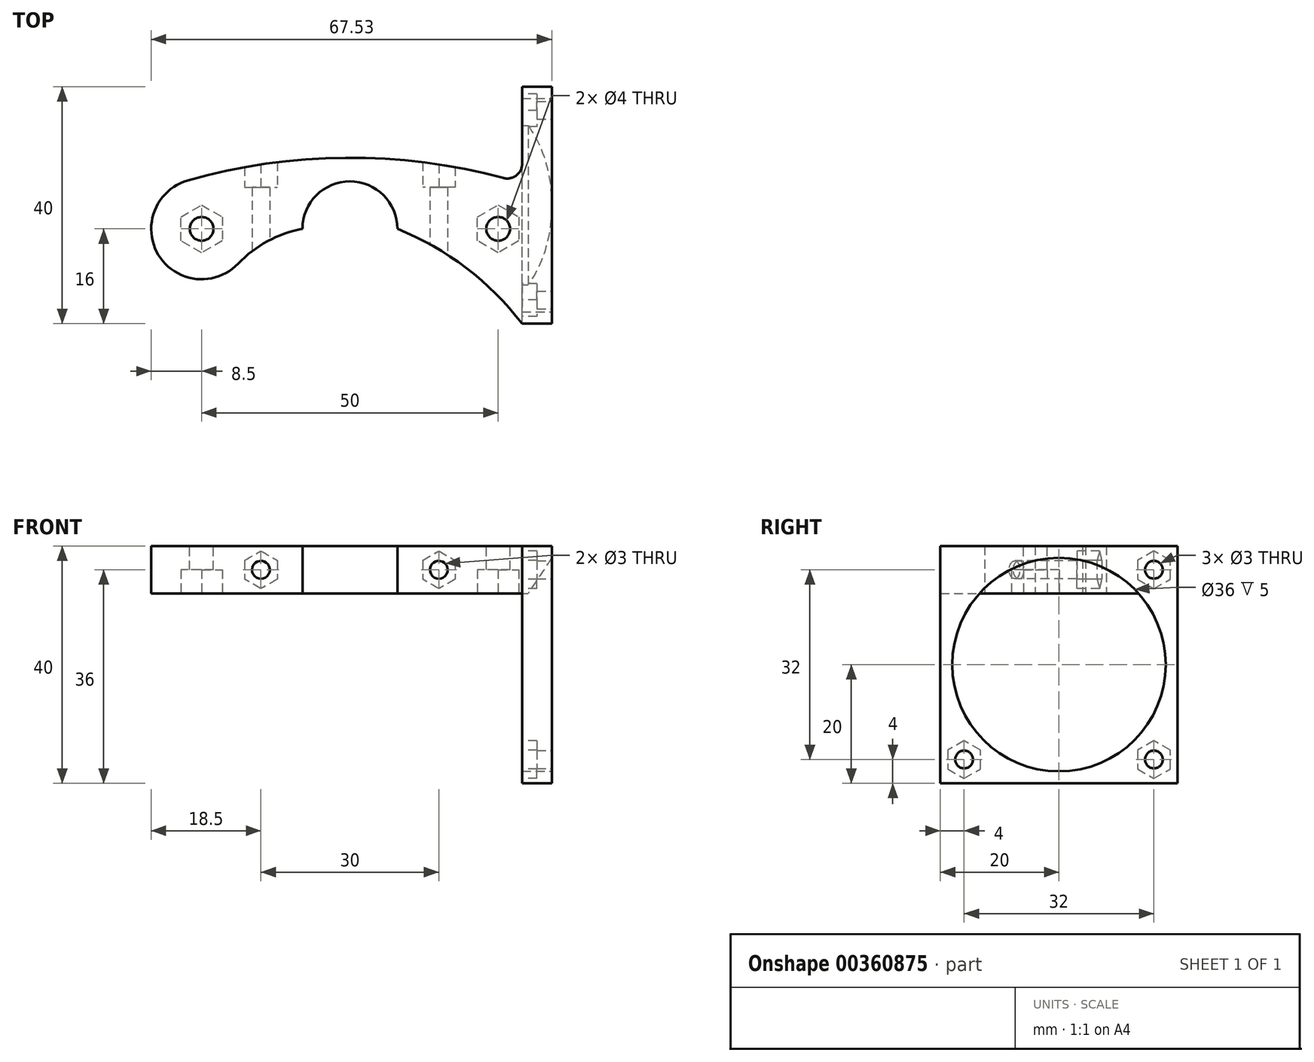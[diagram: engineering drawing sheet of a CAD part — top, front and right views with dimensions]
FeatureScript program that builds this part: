
annotation { "Feature Type Name" : "Feature", "Feature Type Description" : "" }
export const myFeature = defineFeature(function(context is Context, id is Id, definition is map)
    precondition{}
    {
        {
            var Q0;
            Q0=qCreatedBy(makeId("Top.planeOp"),FACE);
            var sketch = newSketch(context, id + "F0", { "sketchPlane" : qUnion([Q0])});
            skArc(sketch, "E0", {"start": v(8, 0) * mm, "mid": v(0, 8) * mm, "end": v(-8, 0) * mm});
            skCircle(sketch, "E1.cCircle", {"center": v(-25, 0) * mm, "radius": 3.5 * mm, "construction": true});
            skLineSegment(sketch, "E1.0", {"start": v(-21.5, 2.02) * mm, "end": v(-21.5, -2.02) * mm});
            skLineSegment(sketch, "E1.1", {"start": v(-21.5, -2.02) * mm, "end": v(-25, -4.04) * mm});
            skLineSegment(sketch, "E1.2", {"start": v(-25, -4.04) * mm, "end": v(-28.5, -2.02) * mm});
            skLineSegment(sketch, "E1.3", {"start": v(-28.5, -2.02) * mm, "end": v(-28.5, 2.02) * mm});
            skLineSegment(sketch, "E1.4", {"start": v(-28.5, 2.02) * mm, "end": v(-25, 4.04) * mm});
            skLineSegment(sketch, "E1.5", {"start": v(-25, 4.04) * mm, "end": v(-21.5, 2.02) * mm});
            skPoint(sketch, "E1.0.midPoint", {"position": v(-21.5, 0) * mm});
            skCircle(sketch, "E2.cCircle", {"center": v(25, 0) * mm, "radius": 3.5 * mm, "construction": true});
            skLineSegment(sketch, "E2.0", {"start": v(28.5, 2.02) * mm, "end": v(28.5, -2.02) * mm});
            skLineSegment(sketch, "E2.1", {"start": v(28.5, -2.02) * mm, "end": v(25, -4.04) * mm});
            skLineSegment(sketch, "E2.2", {"start": v(25, -4.04) * mm, "end": v(21.5, -2.02) * mm});
            skLineSegment(sketch, "E2.3", {"start": v(21.5, -2.02) * mm, "end": v(21.5, 2.02) * mm});
            skLineSegment(sketch, "E2.4", {"start": v(21.5, 2.02) * mm, "end": v(25, 4.04) * mm});
            skLineSegment(sketch, "E2.5", {"start": v(25, 4.04) * mm, "end": v(28.5, 2.02) * mm});
            skPoint(sketch, "E2.0.midPoint", {"position": v(28.5, 0) * mm});
            skCircle(sketch, "E3", {"center": v(-25, 0) * mm, "radius": 8.5 * mm});
            skCircle(sketch, "E4", {"center": v(25, 0) * mm, "radius": 8.5 * mm});
            skLineSegment(sketch, "E5", {"start": v(0, 0) * mm, "end": v(0, 12) * mm});
            skArc(sketch, "E6", {"start": v(27.33, 8.17) * mm, "mid": v(0, 12) * mm, "end": v(-27.33, 8.17) * mm});
            skPoint(sketch, "E6.first.point", {"position": v(-27.33, 8.17) * mm});
            skPoint(sketch, "E6.second.point", {"position": v(27.33, 8.17) * mm});
            skLineSegment(sketch, "E7.bottom", {"start": v(29.03, 24) * mm, "end": v(34.03, 24) * mm});
            skLineSegment(sketch, "E7.top", {"start": v(29.03, -16) * mm, "end": v(34.03, -16) * mm});
            skLineSegment(sketch, "E7.left", {"start": v(29.03, 24) * mm, "end": v(29.03, -16) * mm});
            skLineSegment(sketch, "E7.right", {"start": v(34.03, 24) * mm, "end": v(34.03, -16) * mm});
            skArc(sketch, "E8", {"start": v(29.03, -16) * mm, "mid": v(19.6, -6.57) * mm, "end": v(8, 0) * mm});
            skPoint(sketch, "E8.third.point", {"position": v(19.9, -6.8) * mm});
            skArc(sketch, "E9", {"start": v(25.88, 8.58) * mm, "mid": v(28.05, 9) * mm, "end": v(29.03, 11) * mm});
            skArc(sketch, "E10", {"start": v(-8, 0) * mm, "mid": v(-13.89, -2.08) * mm, "end": v(-18.85, -5.87) * mm});
            skSolve(sketch);
        }
        {
            var Q0;
            Q0 = qSketchRegion(id + "F0", true);
            var Q1;
            {var subQ0=sQuery(id+"F0.wireOp",EDGE,"E7.left");var subQ1=sQuery(id+"F0.wireOp",EDGE,"E4");var subQ2=makeQuery(id+"F0.imprint","INTERSECT",VERTEX,{"disambiguationData":[OD(0.0)],"derivedFrom":[subQ1,subQ0]});Q1=makeQuery(id+"F0.imprint","IMPRINT",FACE,{"disambiguationData":[TD([[makeQuery(id+"F0.imprint","IMPRINT",EDGE,{"disambiguationData":[TD([[subQ2,1.0]])],"derivedFrom":subQ1}),1.0]])]});}
            extrude(context, id + "F1", {"entities" : qUnion([Q0, Q1]), "depth" : 8 * mm});
        }
        {
            var Q0;
            Q0=makeQuery(id+"F1.opExtrude","CAP_FACE",FACE,{"disambiguationData":[OSD([sQuery(id+"F0.wireOp",EDGE,"E0"),sQuery(id+"F0.wireOp",EDGE,"E1.0"),sQuery(id+"F0.wireOp",EDGE,"E1.1"),sQuery(id+"F0.wireOp",EDGE,"E1.2"),sQuery(id+"F0.wireOp",EDGE,"E1.3"),sQuery(id+"F0.wireOp",EDGE,"E1.4"),sQuery(id+"F0.wireOp",EDGE,"E1.5"),sQuery(id+"F0.wireOp",EDGE,"E2.0"),sQuery(id+"F0.wireOp",EDGE,"E2.1"),sQuery(id+"F0.wireOp",EDGE,"E2.2"),sQuery(id+"F0.wireOp",EDGE,"E2.3"),sQuery(id+"F0.wireOp",EDGE,"E2.4"),sQuery(id+"F0.wireOp",EDGE,"E2.5"),sQuery(id+"F0.wireOp",EDGE,"E3"),sQuery(id+"F0.wireOp",EDGE,"E6"),sQuery(id+"F0.wireOp",EDGE,"E7.bottom"),sQuery(id+"F0.wireOp",EDGE,"E7.top"),sQuery(id+"F0.wireOp",EDGE,"E7.left"),sQuery(id+"F0.wireOp",EDGE,"E7.right"),sQuery(id+"F0.wireOp",EDGE,"E8"),sQuery(id+"F0.wireOp",EDGE,"E9"),sQuery(id+"F0.wireOp",EDGE,"E10")])],"isStart":false});
            var sketch = newSketch(context, id + "F2", { "sketchPlane" : qUnion([Q0])});
            skCircle(sketch, "E11.cCircle", {"center": v(25, 0) * mm, "radius": 3.5 * mm, "construction": true});
            skPoint(sketch, "E11.cCircle.centerSnap0", {"position": v(21.5, 0) * mm});
            skLineSegment(sketch, "E11.0", {"start": v(28.5, 2.02) * mm, "end": v(28.5, -2.02) * mm});
            skLineSegment(sketch, "E11.1", {"start": v(28.5, -2.02) * mm, "end": v(25, -4.04) * mm});
            skLineSegment(sketch, "E11.2", {"start": v(25, -4.04) * mm, "end": v(21.5, -2.02) * mm});
            skLineSegment(sketch, "E11.3", {"start": v(21.5, -2.02) * mm, "end": v(21.5, 2.02) * mm});
            skLineSegment(sketch, "E11.4", {"start": v(21.5, 2.02) * mm, "end": v(25, 4.04) * mm});
            skLineSegment(sketch, "E11.5", {"start": v(25, 4.04) * mm, "end": v(28.5, 2.02) * mm});
            skPoint(sketch, "E11.0.midPoint", {"position": v(28.5, 0) * mm});
            skCircle(sketch, "E12.cCircle", {"center": v(-25, 0) * mm, "radius": 3.5 * mm, "construction": true});
            skLineSegment(sketch, "E12.0", {"start": v(-21.5, 2.02) * mm, "end": v(-21.5, -2.02) * mm});
            skLineSegment(sketch, "E12.1", {"start": v(-21.5, -2.02) * mm, "end": v(-25, -4.04) * mm});
            skLineSegment(sketch, "E12.2", {"start": v(-25, -4.04) * mm, "end": v(-28.5, -2.02) * mm});
            skLineSegment(sketch, "E12.3", {"start": v(-28.5, -2.02) * mm, "end": v(-28.5, 2.02) * mm});
            skLineSegment(sketch, "E12.4", {"start": v(-28.5, 2.02) * mm, "end": v(-25, 4.04) * mm});
            skLineSegment(sketch, "E12.5", {"start": v(-25, 4.04) * mm, "end": v(-21.5, 2.02) * mm});
            skPoint(sketch, "E12.0.midPoint", {"position": v(-21.5, 0) * mm});
            skCircle(sketch, "E13", {"center": v(-25, 0) * mm, "radius": 2 * mm});
            skCircle(sketch, "E14", {"center": v(25, 0) * mm, "radius": 2 * mm});
            skSolve(sketch);
        }
        {
            var Q0;
            Q0 = qSketchRegion(id + "F2", true);
            extrude(context, id + "F3", {"entities" : qUnion([Q0]), "operationType" : NewBodyOperationType.ADD, "oppositeDirection" : true, "depth" : 4 * mm});
        }
        {
            var Q0;
            Q0=makeQuery(id+"F1.opExtrude","CAP_FACE",FACE,{"disambiguationData":[OSD([sQuery(id+"F0.wireOp",EDGE,"E0"),sQuery(id+"F0.wireOp",EDGE,"E1.0"),sQuery(id+"F0.wireOp",EDGE,"E1.1"),sQuery(id+"F0.wireOp",EDGE,"E1.2"),sQuery(id+"F0.wireOp",EDGE,"E1.3"),sQuery(id+"F0.wireOp",EDGE,"E1.4"),sQuery(id+"F0.wireOp",EDGE,"E1.5"),sQuery(id+"F0.wireOp",EDGE,"E2.0"),sQuery(id+"F0.wireOp",EDGE,"E2.1"),sQuery(id+"F0.wireOp",EDGE,"E2.2"),sQuery(id+"F0.wireOp",EDGE,"E2.3"),sQuery(id+"F0.wireOp",EDGE,"E2.4"),sQuery(id+"F0.wireOp",EDGE,"E2.5"),sQuery(id+"F0.wireOp",EDGE,"E3"),sQuery(id+"F0.wireOp",EDGE,"E6"),sQuery(id+"F0.wireOp",EDGE,"E7.bottom"),sQuery(id+"F0.wireOp",EDGE,"E7.top"),sQuery(id+"F0.wireOp",EDGE,"E7.left"),sQuery(id+"F0.wireOp",EDGE,"E7.right"),sQuery(id+"F0.wireOp",EDGE,"E8"),sQuery(id+"F0.wireOp",EDGE,"E9"),sQuery(id+"F0.wireOp",EDGE,"E10")])],"isStart":true});
            var sketch = newSketch(context, id + "F4", { "sketchPlane" : qUnion([Q0])});
            skLineSegment(sketch, "E15.bottom", {"start": v(29.03, 16) * mm, "end": v(34.03, 16) * mm});
            skLineSegment(sketch, "E15.top", {"start": v(29.03, -24) * mm, "end": v(34.03, -24) * mm});
            skLineSegment(sketch, "E15.left", {"start": v(29.03, 16) * mm, "end": v(29.03, -24) * mm});
            skLineSegment(sketch, "E15.right", {"start": v(34.03, 16) * mm, "end": v(34.03, -24) * mm});
            skSolve(sketch);
        }
        {
            var Q0;
            Q0 = qSketchRegion(id + "F4", true);
            extrude(context, id + "F5", {"entities" : qUnion([Q0]), "operationType" : NewBodyOperationType.ADD, "depth" : 32 * mm});
        }
        {
            var Q0;
            Q0=makeQuery(id+"F5.boolean.opBoolean","MERGE",FACE,{"derivedFrom":[makeQuery(id+"F1.opExtrude","SWEPT_FACE",FACE,{"disambiguationData":[OSD([sQuery(id+"F0.wireOp",EDGE,"E7.right")])]}),makeQuery(id+"F5.opExtrude","SWEPT_FACE",FACE,{"disambiguationData":[OSD([sQuery(id+"F4.wireOp",EDGE,"E15.right")])]})]});
            var sketch = newSketch(context, id + "F6", { "sketchPlane" : qUnion([Q0])});
            skLineSegment(sketch, "E16", {"start": v(-16, 8) * mm, "end": v(24, -32) * mm});
            skLineSegment(sketch, "E17", {"start": v(24, 8) * mm, "end": v(-16, -32) * mm});
            skCircle(sketch, "E18", {"center": v(4, -12) * mm, "radius": 18 * mm});
            skSolve(sketch);
        }
        {
            var Q0;
            Q0=qCreatedBy(makeId("Front.planeOp"),FACE);
            var sketch = newSketch(context, id + "F7", { "sketchPlane" : qUnion([Q0])});
            skLineSegment(sketch, "E19", {"start": v(-15, 0) * mm, "end": v(-15, 8) * mm});
            skCircle(sketch, "E20", {"center": v(-15, 4) * mm, "radius": 1.5 * mm});
            skPoint(sketch, "E20.perimeterSnap0", {"position": v(-15, 4) * mm});
            skLineSegment(sketch, "E21", {"start": v(15, 0) * mm, "end": v(15, 8) * mm});
            skCircle(sketch, "E22", {"center": v(15, 4) * mm, "radius": 1.5 * mm});
            skPoint(sketch, "E22.perimeterSnap0", {"position": v(15, 4) * mm});
            skSolve(sketch);
        }
        {
            var Q0;
            Q0 = qSketchRegion(id + "F7", true);
            extrude(context, id + "F8", {"entities" : qUnion([Q0]), "operationType" : NewBodyOperationType.REMOVE, "endBound" : BoundingType.SYMMETRIC, "oppositeDirection" : true, "depth" : 25 * mm});
        }
        {
            var Q0;
            Q0=qCreatedBy(makeId("Front.planeOp"),FACE);
            cPlane(context, id + "F9", {"entities" : qUnion([Q0]), "cplaneType" : CPlaneType.OFFSET, "offset" : 7 * mm, "oppositeDirection" : true, "width" : 150 * mm, "height" : 150 * mm});
        }
        {
            var Q0;
            Q0=qCreatedBy(id+"F9.planeOp",FACE);
            var sketch = newSketch(context, id + "F10", { "sketchPlane" : qUnion([Q0])});
            skLineSegment(sketch, "E23", {"start": v(-15, 0) * mm, "end": v(-15, 8) * mm});
            skLineSegment(sketch, "E24", {"start": v(15, 0) * mm, "end": v(15, 8) * mm});
            skCircle(sketch, "E25.cCircle", {"center": v(-15, 4) * mm, "radius": 2.75 * mm, "construction": true});
            skLineSegment(sketch, "E25.0", {"start": v(-12.25, 5.59) * mm, "end": v(-12.25, 2.41) * mm});
            skLineSegment(sketch, "E25.1", {"start": v(-12.25, 2.41) * mm, "end": v(-15, 0.82) * mm});
            skLineSegment(sketch, "E25.2", {"start": v(-15, 0.82) * mm, "end": v(-17.75, 2.41) * mm});
            skLineSegment(sketch, "E25.3", {"start": v(-17.75, 2.41) * mm, "end": v(-17.75, 5.59) * mm});
            skLineSegment(sketch, "E25.4", {"start": v(-17.75, 5.59) * mm, "end": v(-15, 7.18) * mm});
            skLineSegment(sketch, "E25.5", {"start": v(-15, 7.18) * mm, "end": v(-12.25, 5.59) * mm});
            skPoint(sketch, "E25.0.midPoint", {"position": v(-12.25, 4) * mm});
            skCircle(sketch, "E26.cCircle", {"center": v(15, 4) * mm, "radius": 2.75 * mm, "construction": true});
            skLineSegment(sketch, "E26.0", {"start": v(12.25, 2.41) * mm, "end": v(12.25, 5.59) * mm});
            skLineSegment(sketch, "E26.1", {"start": v(12.25, 5.59) * mm, "end": v(15, 7.18) * mm});
            skLineSegment(sketch, "E26.2", {"start": v(15, 7.18) * mm, "end": v(17.75, 5.59) * mm});
            skLineSegment(sketch, "E26.3", {"start": v(17.75, 5.59) * mm, "end": v(17.75, 2.41) * mm});
            skLineSegment(sketch, "E26.4", {"start": v(17.75, 2.41) * mm, "end": v(15, 0.82) * mm});
            skLineSegment(sketch, "E26.5", {"start": v(15, 0.82) * mm, "end": v(12.25, 2.41) * mm});
            skPoint(sketch, "E26.0.midPoint", {"position": v(12.25, 4) * mm});
            skSolve(sketch);
        }
        {
            var Q0;
            Q0 = qSketchRegion(id + "F10", true);
            extrude(context, id + "F11", {"entities" : qUnion([Q0]), "operationType" : NewBodyOperationType.REMOVE, "oppositeDirection" : true, "depth" : 25 * mm});
        }
        {
            var Q0;
            Q0 = qSketchRegion(id + "F6", true);
            extrude(context, id + "F12", {"entities" : qUnion([Q0]), "operationType" : NewBodyOperationType.REMOVE, "oppositeDirection" : true, "depth" : 5 * mm});
        }
        {
            var Q0;
            Q0=makeQuery(id+"F5.boolean.opBoolean","MERGE",FACE,{"derivedFrom":[makeQuery(id+"F1.opExtrude","SWEPT_FACE",FACE,{"disambiguationData":[OSD([sQuery(id+"F0.wireOp",EDGE,"E7.top")])]}),makeQuery(id+"F5.opExtrude","SWEPT_FACE",FACE,{"disambiguationData":[OSD([sQuery(id+"F4.wireOp",EDGE,"E15.bottom")])]})]});
            var sketch = newSketch(context, id + "F13", { "sketchPlane" : qUnion([Q0])});
            skLineSegment(sketch, "E27", {"start": v(34.03, 8) * mm, "end": v(34.03, 6) * mm});
            skLineSegment(sketch, "E28", {"start": v(29.03, 0) * mm, "end": v(30.03, 0) * mm});
            skLineSegment(sketch, "E29", {"start": v(30.03, 0) * mm, "end": v(34.03, 6) * mm});
            skSolve(sketch);
        }
        {
            var Q0;
            Q0 = qSketchRegion(id + "F13", true);
            var Q1;
            Q1=makeQuery(id+"F13.imprint","IMPRINT",FACE,{"disambiguationData":[TD([[makeQuery(id+"F13.imprint","IMPRINT",EDGE,{"derivedFrom":sQuery(id+"F13.wireOp",EDGE,"E27")}),-1.0]])]});
            extrude(context, id + "F14", {"entities" : qUnion([Q0, Q1]), "operationType" : NewBodyOperationType.ADD, "oppositeDirection" : true, "depth" : 40 * mm});
        }
        {
            var Q0;
            Q0=makeQuery(id+"F5.boolean.opBoolean","MERGE",FACE,{"derivedFrom":[makeQuery(id+"F1.opExtrude","SWEPT_FACE",FACE,{"disambiguationData":[OSD([sQuery(id+"F0.wireOp",EDGE,"E7.right")])]}),makeQuery(id+"F5.opExtrude","SWEPT_FACE",FACE,{"disambiguationData":[OSD([sQuery(id+"F4.wireOp",EDGE,"E15.right")])]})]});
            var sketch = newSketch(context, id + "F15", { "sketchPlane" : qUnion([Q0])});
            skLineSegment(sketch, "E30", {"start": v(24, 8) * mm, "end": v(-16, -32) * mm});
            skLineSegment(sketch, "E31", {"start": v(-16, 8) * mm, "end": v(24, -32) * mm});
            skCircle(sketch, "E32", {"center": v(20, 4) * mm, "radius": 1.5 * mm});
            skCircle(sketch, "E33", {"center": v(20, -28) * mm, "radius": 1.5 * mm});
            skCircle(sketch, "E34", {"center": v(-12, -28) * mm, "radius": 1.5 * mm});
            skSolve(sketch);
        }
        {
            var Q0;
            Q0 = qSketchRegion(id + "F15", true);
            extrude(context, id + "F16", {"entities" : qUnion([Q0]), "operationType" : NewBodyOperationType.REMOVE, "oppositeDirection" : true, "depth" : 5 * mm});
        }
        {
            var Q0;
            {var subQ0=sQuery(id+"F0.wireOp",EDGE,"E7.left");Q0=makeQuery(id+"F14.boolean.opBoolean","MERGE",FACE,{"derivedFrom":[makeQuery(id+"F5.boolean.opBoolean","MERGE",FACE,{"derivedFrom":[makeQuery(id+"F1.opExtrude","SWEPT_FACE",FACE,{"disambiguationData":[OSD([subQ0])]}),makeQuery(id+"F5.opExtrude","SWEPT_FACE",FACE,{"disambiguationData":[OSD([sQuery(id+"F4.wireOp",EDGE,"E15.left")])]})]}),makeQuery(id+"F14.opExtrude","SWEPT_FACE",FACE,{"disambiguationData":[OSD([sQuery(id+"F0.wireOp",EDGE,"E7.top"),subQ0,sQuery(id+"F0.wireOp",EDGE,"E8")])]})]});}
            var sketch = newSketch(context, id + "F17", { "sketchPlane" : qUnion([Q0])});
            skCircle(sketch, "E35.cCircle", {"center": v(-20, -28) * mm, "radius": 2.75 * mm, "construction": true});
            skLineSegment(sketch, "E35.0", {"start": v(-17.25, -26.41) * mm, "end": v(-17.25, -29.59) * mm});
            skLineSegment(sketch, "E35.1", {"start": v(-17.25, -29.59) * mm, "end": v(-20, -31.18) * mm});
            skLineSegment(sketch, "E35.2", {"start": v(-20, -31.18) * mm, "end": v(-22.75, -29.59) * mm});
            skLineSegment(sketch, "E35.3", {"start": v(-22.75, -29.59) * mm, "end": v(-22.75, -26.41) * mm});
            skLineSegment(sketch, "E35.4", {"start": v(-22.75, -26.41) * mm, "end": v(-20, -24.82) * mm});
            skLineSegment(sketch, "E35.5", {"start": v(-20, -24.82) * mm, "end": v(-17.25, -26.41) * mm});
            skPoint(sketch, "E35.0.midPoint", {"position": v(-17.25, -28) * mm});
            skCircle(sketch, "E36.cCircle", {"center": v(12, -28) * mm, "radius": 2.75 * mm, "construction": true});
            skLineSegment(sketch, "E36.0", {"start": v(14.75, -26.41) * mm, "end": v(14.75, -29.59) * mm});
            skLineSegment(sketch, "E36.1", {"start": v(14.75, -29.59) * mm, "end": v(12, -31.18) * mm});
            skLineSegment(sketch, "E36.2", {"start": v(12, -31.18) * mm, "end": v(9.25, -29.59) * mm});
            skLineSegment(sketch, "E36.3", {"start": v(9.25, -29.59) * mm, "end": v(9.25, -26.41) * mm});
            skLineSegment(sketch, "E36.4", {"start": v(9.25, -26.41) * mm, "end": v(12, -24.82) * mm});
            skLineSegment(sketch, "E36.5", {"start": v(12, -24.82) * mm, "end": v(14.75, -26.41) * mm});
            skPoint(sketch, "E36.0.midPoint", {"position": v(14.75, -28) * mm});
            skCircle(sketch, "E37.cCircle", {"center": v(-20, 4) * mm, "radius": 2.75 * mm, "construction": true});
            skLineSegment(sketch, "E37.0", {"start": v(-17.25, 5.59) * mm, "end": v(-17.25, 2.41) * mm});
            skLineSegment(sketch, "E37.1", {"start": v(-17.25, 2.41) * mm, "end": v(-20, 0.82) * mm});
            skLineSegment(sketch, "E37.2", {"start": v(-20, 0.82) * mm, "end": v(-22.75, 2.41) * mm});
            skLineSegment(sketch, "E37.3", {"start": v(-22.75, 2.41) * mm, "end": v(-22.75, 5.59) * mm});
            skLineSegment(sketch, "E37.4", {"start": v(-22.75, 5.59) * mm, "end": v(-20, 7.18) * mm});
            skLineSegment(sketch, "E37.5", {"start": v(-20, 7.18) * mm, "end": v(-17.25, 5.59) * mm});
            skPoint(sketch, "E37.0.midPoint", {"position": v(-17.25, 4) * mm});
            skSolve(sketch);
        }
        {
            var Q0;
            Q0 = qSketchRegion(id + "F17", true);
            extrude(context, id + "F18", {"entities" : qUnion([Q0]), "operationType" : NewBodyOperationType.REMOVE, "oppositeDirection" : true, "depth" : 2.5 * mm});
        }
    });
